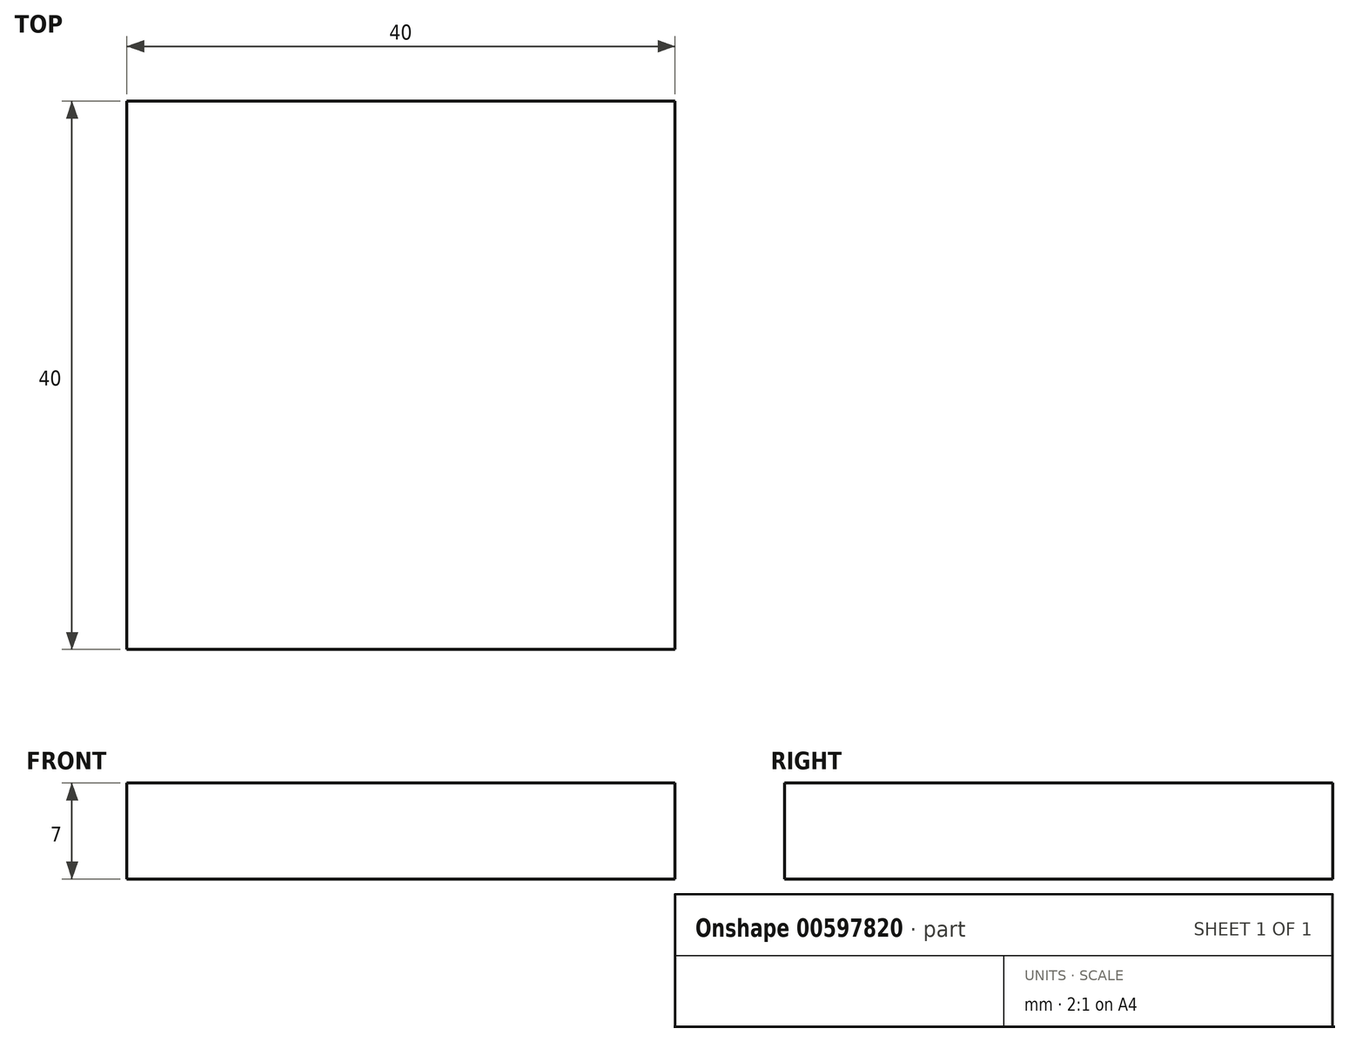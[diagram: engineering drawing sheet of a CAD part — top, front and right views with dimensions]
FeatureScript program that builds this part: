
annotation { "Feature Type Name" : "Feature", "Feature Type Description" : "" }
export const myFeature = defineFeature(function(context is Context, id is Id, definition is map)
    precondition{}
    {
        {
            var Q0;
            Q0=qCreatedBy(makeId("Top.planeOp"),FACE);
            var sketch = newSketch(context, id + "F0", { "sketchPlane" : qUnion([Q0])});
            skLineSegment(sketch, "E0.bottom", {"start": v(-20, -20) * mm, "end": v(20, -20) * mm});
            skLineSegment(sketch, "E0.top", {"start": v(-20, 20) * mm, "end": v(20, 20) * mm});
            skLineSegment(sketch, "E0.left", {"start": v(-20, -20) * mm, "end": v(-20, 20) * mm});
            skLineSegment(sketch, "E0.right", {"start": v(20, -20) * mm, "end": v(20, 20) * mm});
            skPoint(sketch, "E1", {"position": v(0, 20) * mm});
            skPoint(sketch, "E2", {"position": v(20, 0) * mm});
            skSolve(sketch);
        }
        {
            var Q0;
            Q0 = qSketchRegion(id + "F0", true);
            extrude(context, id + "F1", {"entities" : qUnion([Q0]), "depth" : 7 * mm, "offsetDistance" : 25 * mm});
        }
    });
